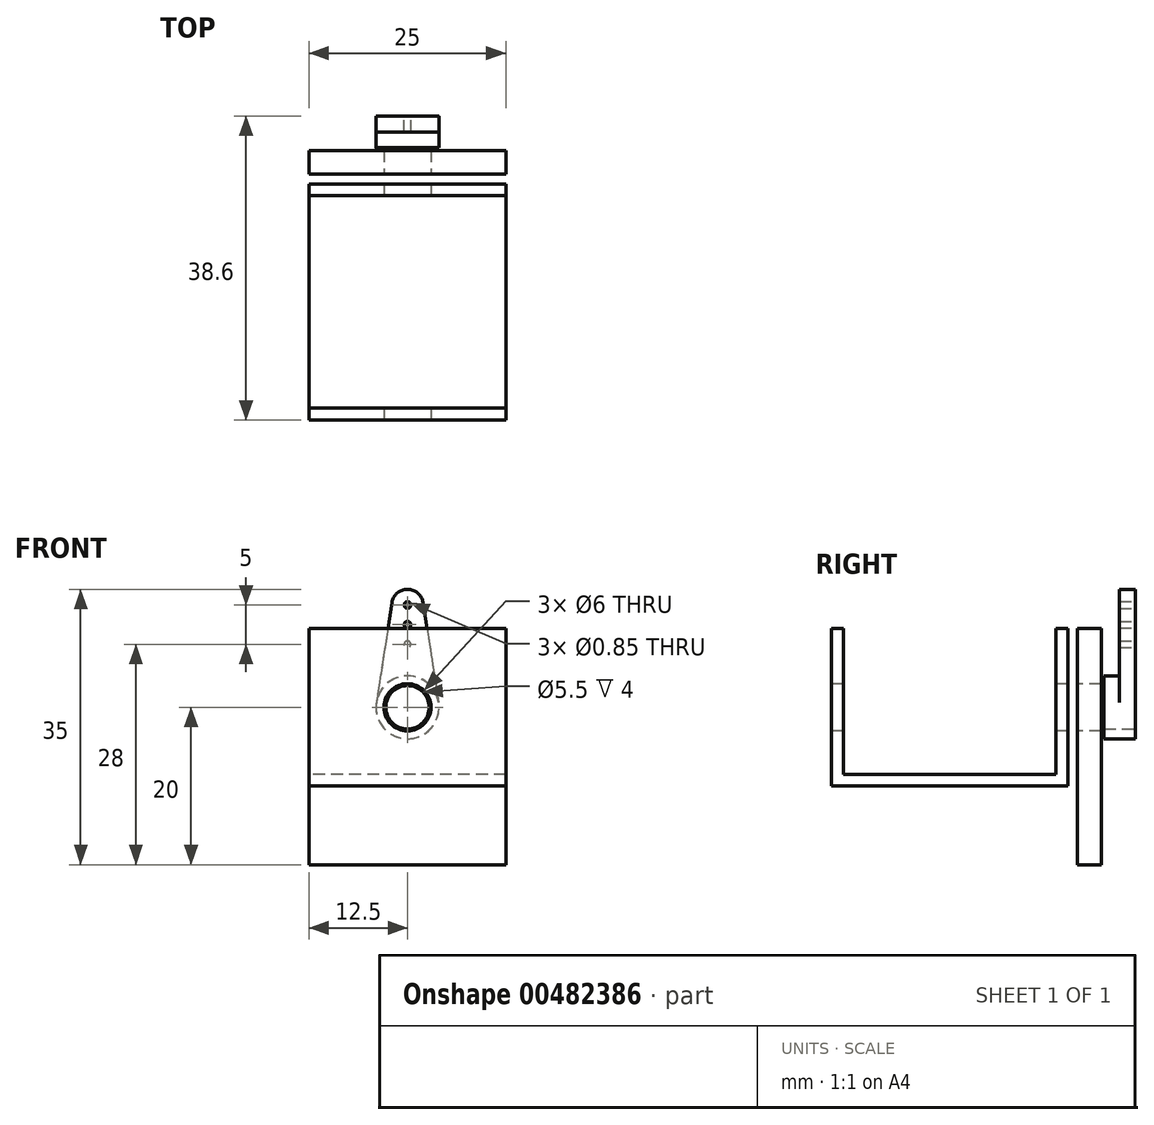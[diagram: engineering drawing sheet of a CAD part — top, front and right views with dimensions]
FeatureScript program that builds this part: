
annotation { "Feature Type Name" : "Feature", "Feature Type Description" : "" }
export const myFeature = defineFeature(function(context is Context, id is Id, definition is map)
    precondition{}
    {
        {
            var Q0;
            Q0=qCreatedBy(makeId("Front.planeOp"),FACE);
            var sketch = newSketch(context, id + "F0", { "sketchPlane" : qUnion([Q0])});
            skCircle(sketch, "E0", {"center": v(0, 0) * mm, "radius": 4 * mm});
            skCircle(sketch, "E1", {"center": v(0, 13) * mm, "radius": 2 * mm});
            skLineSegment(sketch, "E2", {"start": v(-1.98, 13.3) * mm, "end": v(-3.95, 0.62) * mm});
            skLineSegment(sketch, "E3", {"start": v(1.98, 13.3) * mm, "end": v(3.95, 0.62) * mm});
            skLineSegment(sketch, "E4", {"start": v(0, 13) * mm, "end": v(0, 0) * mm, "construction": true});
            skCircle(sketch, "E5", {"center": v(0, 0) * mm, "radius": 2.75 * mm});
            skCircle(sketch, "E6.0.1.0", {"center": v(0, 10.5) * mm, "radius": 0.42 * mm});
            skLineSegment(sketch, "E6.direction2", {"start": v(0, 13) * mm, "end": v(0, 10.5) * mm, "construction": true});
            skCircle(sketch, "E7.0.1.0", {"center": v(0, 8) * mm, "radius": 0.42 * mm});
            skLineSegment(sketch, "E8", {"start": v(0, 10.5) * mm, "end": v(0, 8) * mm, "construction": true});
            skCircle(sketch, "E9", {"center": v(0, 13) * mm, "radius": 0.42 * mm});
            skSolve(sketch);
        }
        {
            var Q0;
            {var subQ0=sQuery(id+"F0.wireOp",EDGE,"E2");Q0=makeQuery(id+"F0.imprint","IMPRINT",FACE,{"disambiguationData":[TD([[makeQuery(id+"F0.imprint","IMPRINT",EDGE,{"derivedFrom":subQ0}),1.0]])]});}
            var Q1;
            Q1=makeQuery(id+"F0.imprint","IMPRINT",FACE,{"disambiguationData":[TD([[makeQuery(id+"F0.imprint","IMPRINT",EDGE,{"derivedFrom":sQuery(id+"F0.wireOp",EDGE,"E9")}),-1.0]])]});
            extrude(context, id + "F1", {"entities" : qUnion([Q0, Q1]), "depth" : 2 * mm});
        }
        {
            var Q0;
            Q0=makeQuery(id+"F0.imprint","IMPRINT",FACE,{"disambiguationData":[TD([[makeQuery(id+"F0.imprint","IMPRINT",EDGE,{"derivedFrom":sQuery(id+"F0.wireOp",EDGE,"E5")}),-1.0]])]});
            extrude(context, id + "F2", {"entities" : qUnion([Q0]), "operationType" : NewBodyOperationType.ADD, "depth" : 4 * mm});
        }
        {
            var Q0;
            Q0=qCreatedBy(makeId("Right.planeOp"),FACE);
            var sketch = newSketch(context, id + "F3", { "sketchPlane" : qUnion([Q0])});
            skLineSegment(sketch, "E10", {"start": v(23.98, 0) * mm, "end": v(-34.81, 0) * mm, "construction": true});
            skLineSegment(sketch, "E11.bottom", {"start": v(-38.6, 10) * mm, "end": v(-8.6, 10) * mm});
            skLineSegment(sketch, "E11.top", {"start": v(-38.6, -10) * mm, "end": v(-8.6, -10) * mm});
            skLineSegment(sketch, "E11.left", {"start": v(-38.6, 10) * mm, "end": v(-38.6, -10) * mm});
            skLineSegment(sketch, "E11.right", {"start": v(-8.6, 10) * mm, "end": v(-8.6, -10) * mm});
            skLineSegment(sketch, "E12.bottom", {"start": v(-7.35, 10) * mm, "end": v(-4.35, 10) * mm});
            skLineSegment(sketch, "E12.top", {"start": v(-7.35, -20) * mm, "end": v(-4.35, -20) * mm});
            skLineSegment(sketch, "E12.left", {"start": v(-7.35, 10) * mm, "end": v(-7.35, -20) * mm});
            skLineSegment(sketch, "E12.right", {"start": v(-4.35, 10) * mm, "end": v(-4.35, -20) * mm});
            skSolve(sketch);
        }
        {
            var Q0;
            Q0=makeQuery(id+"F3.imprint","IMPRINT",FACE,{"disambiguationData":[TD([[makeQuery(id+"F3.imprint","IMPRINT",EDGE,{"derivedFrom":sQuery(id+"F3.wireOp",EDGE,"E11.bottom")}),-1.0]])]});
            extrude(context, id + "F4", {"entities" : qUnion([Q0]), "endBound" : BoundingType.SYMMETRIC, "depth" : 25 * mm});
        }
        {
            var Q0;
            Q0=makeQuery(id+"F4.opExtrude","CAP_FACE",FACE,{"disambiguationData":[OSD([sQuery(id+"F3.wireOp",EDGE,"E11.bottom"),sQuery(id+"F3.wireOp",EDGE,"E11.top"),sQuery(id+"F3.wireOp",EDGE,"E11.left"),sQuery(id+"F3.wireOp",EDGE,"E11.right")])],"isStart":false});
            var Q1;
            Q1=makeQuery(id+"F4.opExtrude","SWEPT_FACE",FACE,{"disambiguationData":[OSD([sQuery(id+"F3.wireOp",EDGE,"E11.bottom")])]});
            var Q2;
            Q2=makeQuery(id+"F4.opExtrude","CAP_FACE",FACE,{"disambiguationData":[OSD([sQuery(id+"F3.wireOp",EDGE,"E11.bottom"),sQuery(id+"F3.wireOp",EDGE,"E11.top"),sQuery(id+"F3.wireOp",EDGE,"E11.left"),sQuery(id+"F3.wireOp",EDGE,"E11.right")])],"isStart":true});
            shell(context, id + "F5", {"entities" : qUnion([Q0, Q1, Q2]), "thickness" : 1.5 * mm});
        }
        {
            var Q0;
            Q0=makeQuery(id+"F3.imprint","IMPRINT",FACE,{"disambiguationData":[TD([[makeQuery(id+"F3.imprint","IMPRINT",EDGE,{"derivedFrom":sQuery(id+"F3.wireOp",EDGE,"E12.bottom")}),-1.0]])]});
            extrude(context, id + "F6", {"entities" : qUnion([Q0]), "endBound" : BoundingType.SYMMETRIC, "depth" : 25 * mm});
        }
        {
            var Q0;
            Q0=makeQuery(id+"F4.opExtrude","SWEPT_FACE",FACE,{"disambiguationData":[OSD([sQuery(id+"F3.wireOp",EDGE,"E11.left")])]});
            var sketch = newSketch(context, id + "F7", { "sketchPlane" : qUnion([Q0])});
            skCircle(sketch, "E13", {"center": v(0, 0) * mm, "radius": 3 * mm});
            skSolve(sketch);
        }
        {
            var Q0;
            Q0=makeQuery(id+"F7.imprint","IMPRINT",FACE,{"disambiguationData":[TD([[makeQuery(id+"F7.imprint","IMPRINT",EDGE,{"derivedFrom":sQuery(id+"F7.wireOp",EDGE,"E13")}),1.0]])]});
            extrude(context, id + "F8", {"entities" : qUnion([Q0]), "endBound" : BoundingType.THROUGH_ALL, "oppositeDirection" : true, "depth" : 25 * mm});
        }
        {
            var Q0;
            Q0=makeQuery(id+"F8.opExtrude","SWEPT_BODY",BODY,{"disambiguationData":[OSD([sQuery(id+"F7.wireOp",EDGE,"E13")])]});
            var Q1;
            Q1=makeQuery(id+"F4.opExtrude","SWEPT_BODY",BODY,{"disambiguationData":[OSD([sQuery(id+"F3.wireOp",EDGE,"E11.bottom"),sQuery(id+"F3.wireOp",EDGE,"E11.top"),sQuery(id+"F3.wireOp",EDGE,"E11.left"),sQuery(id+"F3.wireOp",EDGE,"E11.right")])]});
            var Q2;
            Q2=makeQuery(id+"F6.opExtrude","SWEPT_BODY",BODY,{"disambiguationData":[OSD([sQuery(id+"F3.wireOp",EDGE,"E12.bottom"),sQuery(id+"F3.wireOp",EDGE,"E12.top"),sQuery(id+"F3.wireOp",EDGE,"E12.left"),sQuery(id+"F3.wireOp",EDGE,"E12.right")])]});
            booleanBodies(context, id + "F9", {"operationType" : BooleanOperationType.SUBTRACTION, "tools" : qUnion([Q0]), "targets" : qUnion([Q1, Q2])});
        }
    });
